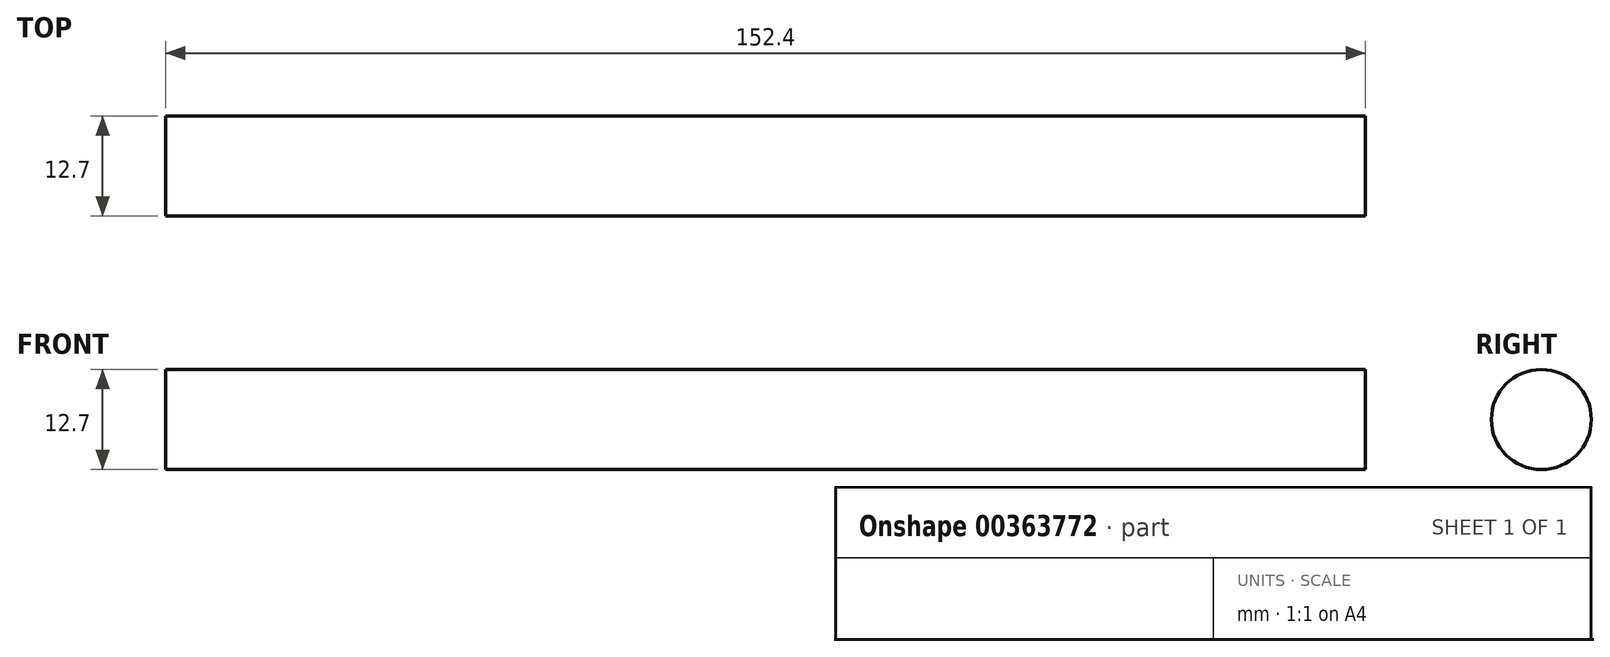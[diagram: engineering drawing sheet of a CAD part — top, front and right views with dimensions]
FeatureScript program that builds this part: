
annotation { "Feature Type Name" : "Feature", "Feature Type Description" : "" }
export const myFeature = defineFeature(function(context is Context, id is Id, definition is map)
    precondition{}
    {
        {
            var Q0;
            Q0=qCreatedBy(makeId("Right.planeOp"),FACE);
            var sketch = newSketch(context, id + "F0", { "sketchPlane" : qUnion([Q0])});
            skCircle(sketch, "E0", {"center": v(0, 0) * mm, "radius": 6.35 * mm});
            skSolve(sketch);
        }
        {
            var Q0;
            Q0=makeQuery(id+"F0.imprint","IMPRINT",FACE,{"disambiguationData":[TD([[makeQuery(id+"F0.imprint","IMPRINT",EDGE,{"derivedFrom":sQuery(id+"F0.wireOp",EDGE,"E0")}),1.0]])]});
            extrude(context, id + "F1", {"entities" : qUnion([Q0]), "depth" : 76.2 * mm, "hasSecondDirection" : true, "secondDirectionOppositeDirection" : true, "secondDirectionDepth" : 76.2 * mm});
        }
    });
